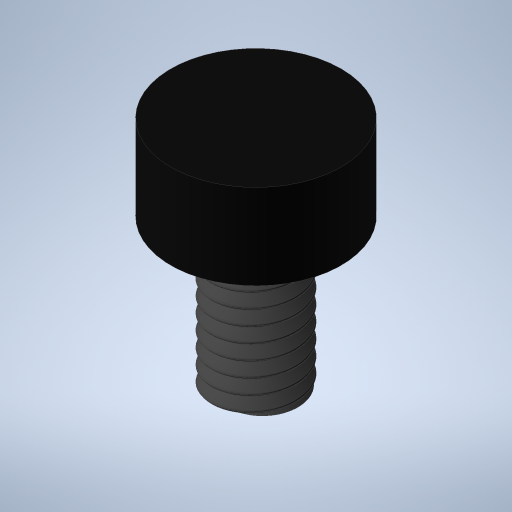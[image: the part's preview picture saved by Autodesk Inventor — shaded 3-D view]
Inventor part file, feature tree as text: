
AUTODESK INVENTOR PART (.ipt)
format: ipt  version: 2023 (Build 270158000, 158)  size: 731,136 bytes
history: native  units: in
note: dims shown in document units (in); Inventor stores cm internally (conversion verified against a paired STEP export)
features: sketch x4, revolve x3, thread x1, helix x1
ambient origin geometry x8: Origin, YZ Plane, XZ Plane, XY Plane, X Axis, Y Axis, Z Axis, Center Point
bodies: Solid1 (feature_tree), Solid4 (feature_tree)
feature tree (9):
  revolve  "Revolution1"  [1 undecoded]
  thread  "Thread3"  [1 undecoded]
  revolve  "Revolution6"  Angle=90.0deg
  revolve  "Revolution7"  [1 undecoded]
  helix  "Coil3"  [1 undecoded]
  sketch  "Sketch1"  dims[d0=0.2756in d1=0.0787in d2=0.1575in]
  sketch  "Sketch8"  dims[d3=0.1575in d4=90.0deg]
  sketch  "Sketch9"  dims[d14=0.3779in d35=0.3779in d47=0.2756in d48=0.0in]
  sketch  "Sketch10"  dims[d49=0.3779in d50=0.0044in d51=0.0044in d54=0.0276in d56=0.3779in d58=0.0in d59=0.0in d60=0.0276in d61=0.3307in d62=0.3937in d63=0.0in d64=0.0in d65=0.0in d66=0.0in d67=0.0in]
note: 4 required parameter values undecoded (feature->parameter linkage not recoverable at this tier; creation-order binding heuristic only, values carry confidence <= 0.55)